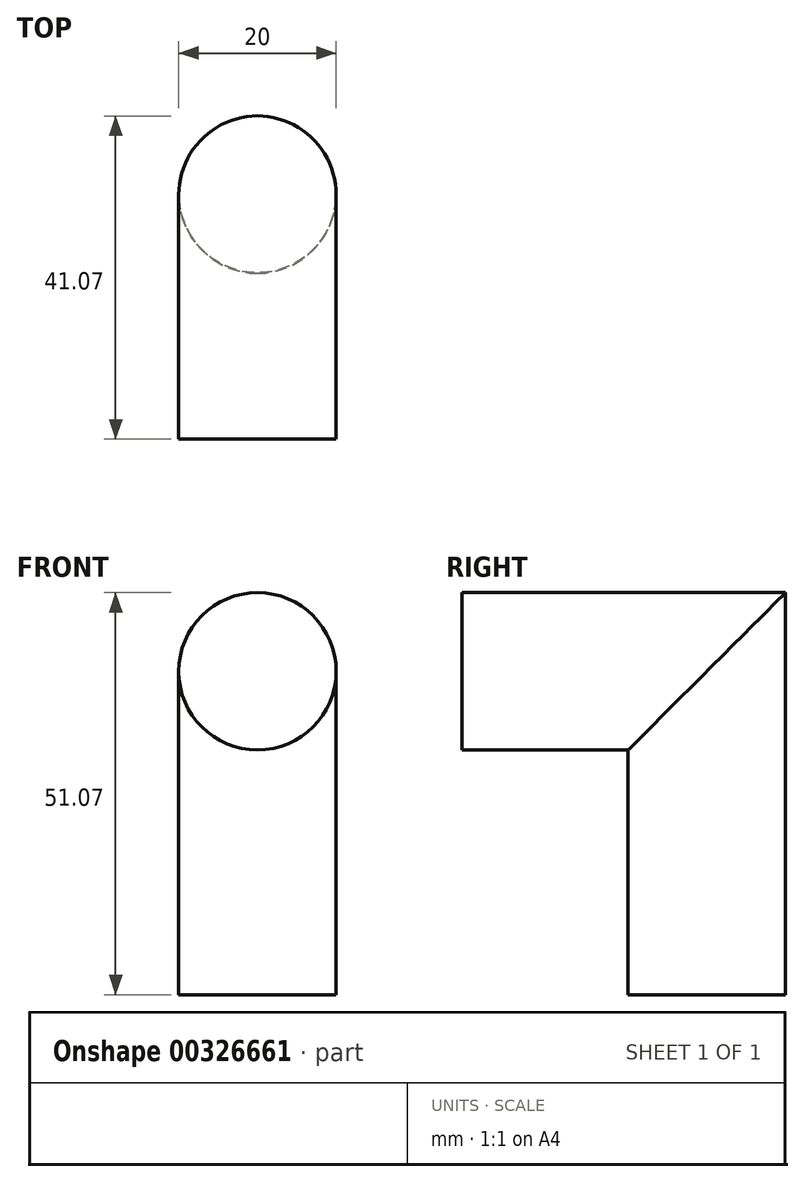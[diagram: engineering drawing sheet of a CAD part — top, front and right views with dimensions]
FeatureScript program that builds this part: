
annotation { "Feature Type Name" : "Feature", "Feature Type Description" : "" }
export const myFeature = defineFeature(function(context is Context, id is Id, definition is map)
    precondition{}
    {
        {
            var Q0;
            Q0=qCreatedBy(makeId("Front.planeOp"),FACE);
            var sketch = newSketch(context, id + "F0", { "sketchPlane" : qUnion([Q0])});
            skPoint(sketch, "E0.visualSharp", {"position": v(0, 30) * mm});
            skCircle(sketch, "E1", {"center": v(0, 30) * mm, "radius": 10 * mm});
            skSolve(sketch);
        }
        {
            var Q0;
            Q0=qCreatedBy(makeId("Right.planeOp"),FACE);
            var sketch = newSketch(context, id + "F1", { "sketchPlane" : qUnion([Q0])});
            skLineSegment(sketch, "E2", {"start": v(0, 28.93) * mm, "end": v(30, 28.93) * mm});
            skLineSegment(sketch, "E3", {"start": v(30, 28.93) * mm, "end": v(30, -11.07) * mm});
            skSolve(sketch);
        }
        {
            var Q0;
            Q0=makeQuery(id+"F0.imprint","IMPRINT",FACE,{"disambiguationData":[TD([[makeQuery(id+"F0.imprint","IMPRINT",EDGE,{"derivedFrom":sQuery(id+"F0.wireOp",EDGE,"E1")}),1.0]])]});
            var Q1;
            Q1=sQuery(id+"F1.wireOp",EDGE,"E2");
            var Q2;
            Q2=sQuery(id+"F1.wireOp",EDGE,"E3");
            sweep(context, id + "F2", {"profiles" : qUnion([Q0]), "path" : qUnion([Q1, Q2])});
        }
    });
